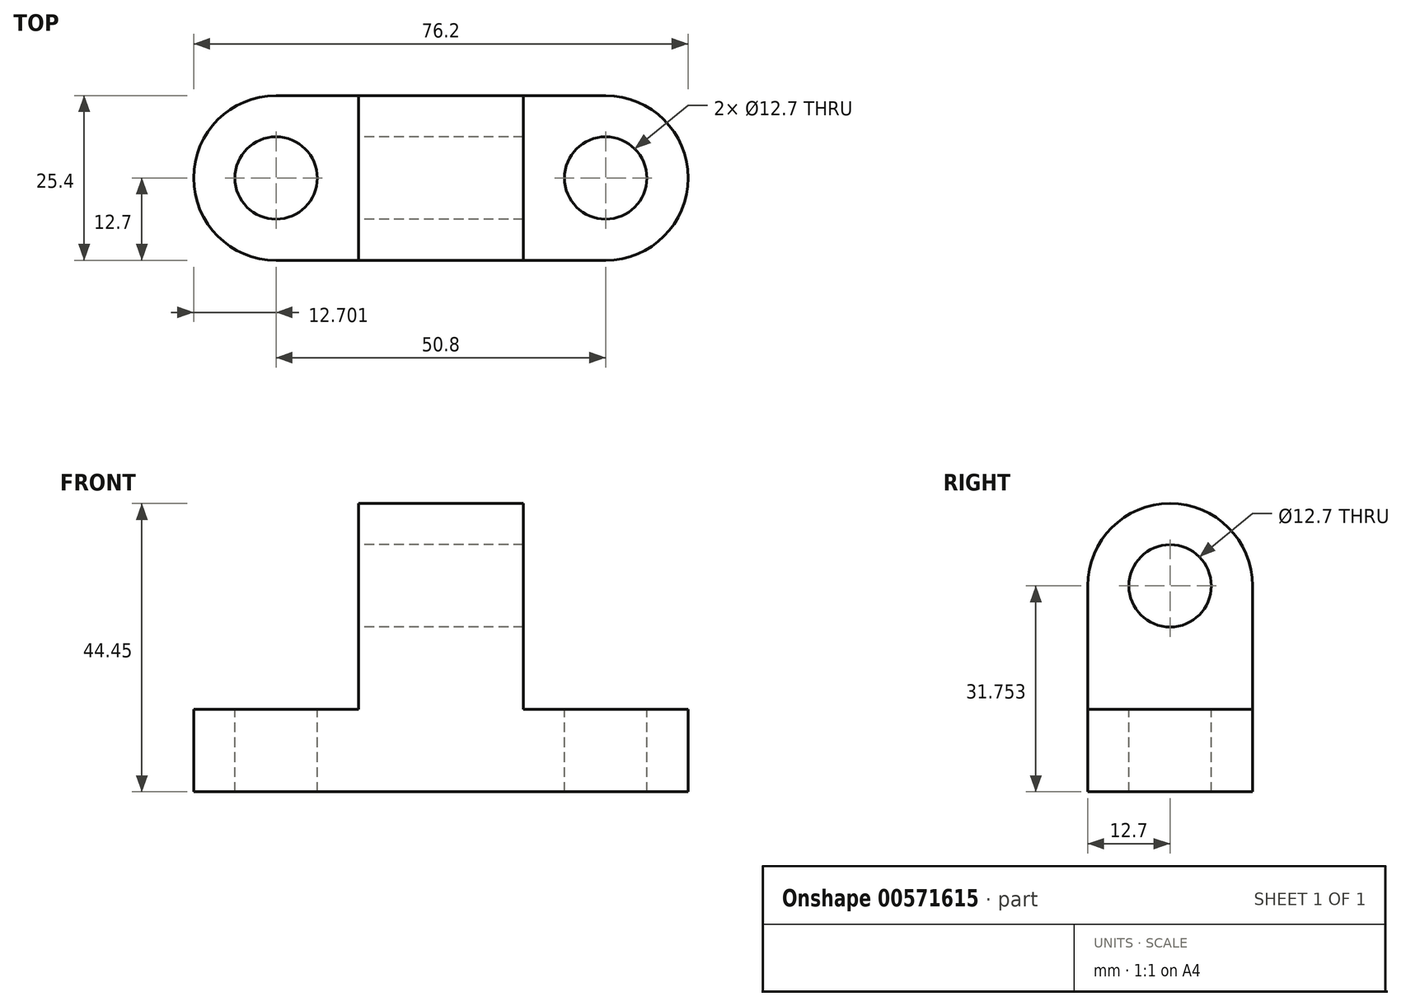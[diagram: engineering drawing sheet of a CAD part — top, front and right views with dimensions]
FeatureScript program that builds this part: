
annotation { "Feature Type Name" : "Feature", "Feature Type Description" : "" }
export const myFeature = defineFeature(function(context is Context, id is Id, definition is map)
    precondition{}
    {
        {
            var Q0;
            Q0=qCreatedBy(makeId("Front.planeOp"),FACE);
            var sketch = newSketch(context, id + "F0", { "sketchPlane" : qUnion([Q0])});
            skLineSegment(sketch, "E0", {"start": v(-37.6, -9.17) * mm, "end": v(13.2, -9.17) * mm});
            skLineSegment(sketch, "E1", {"start": v(13.2, -9.17) * mm, "end": v(13.2, 3.53) * mm});
            skLineSegment(sketch, "E2", {"start": v(13.2, 3.53) * mm, "end": v(0.5, 3.53) * mm});
            skLineSegment(sketch, "E3", {"start": v(0.5, 3.53) * mm, "end": v(0.5, 22.58) * mm});
            skLineSegment(sketch, "E4", {"start": v(0.5, 22.58) * mm, "end": v(-24.9, 22.58) * mm});
            skLineSegment(sketch, "E5", {"start": v(-24.9, 22.58) * mm, "end": v(-24.9, 3.53) * mm});
            skLineSegment(sketch, "E6", {"start": v(-24.9, 3.53) * mm, "end": v(-37.6, 3.53) * mm});
            skLineSegment(sketch, "E7", {"start": v(-37.6, 3.53) * mm, "end": v(-37.6, -9.17) * mm});
            skSolve(sketch);
        }
        {
            var Q0;
            Q0 = qSketchRegion(id + "F0", true);
            extrude(context, id + "F1", {"entities" : qUnion([Q0]), "depth" : 25.4 * mm, "offsetDistance" : 25.4 * mm});
        }
        {
            var Q0;
            Q0=makeQuery(id+"F1.opExtrude","SWEPT_FACE",FACE,{"disambiguationData":[OSD([sQuery(id+"F0.wireOp",EDGE,"E2")])]});
            var sketch = newSketch(context, id + "F2", { "sketchPlane" : qUnion([Q0])});
            skArc(sketch, "E8", {"start": v(13.2, -25.4) * mm, "mid": v(25.9, -12.7) * mm, "end": v(13.2, 0) * mm});
            skSolve(sketch);
        }
        {
            var Q0;
            Q0=makeQuery(id+"F2.imprint","IMPRINT",FACE,{"disambiguationData":[TD([[makeQuery(id+"F2.imprint","IMPRINT",EDGE,{"derivedFrom":sQuery(id+"F2.wireOp",EDGE,"E8")}),1.0]])]});
            extrude(context, id + "F3", {"entities" : qUnion([Q0]), "operationType" : NewBodyOperationType.ADD, "oppositeDirection" : true, "depth" : 12.7 * mm, "offsetDistance" : 25.4 * mm});
        }
        {
            var Q0;
            Q0=makeQuery(id+"F1.opExtrude","SWEPT_FACE",FACE,{"disambiguationData":[OSD([sQuery(id+"F0.wireOp",EDGE,"E6")])]});
            var sketch = newSketch(context, id + "F4", { "sketchPlane" : qUnion([Q0])});
            skArc(sketch, "E9", {"start": v(-37.6, 0) * mm, "mid": v(-50.3, -12.7) * mm, "end": v(-37.6, -25.4) * mm});
            skSolve(sketch);
        }
        {
            var Q0;
            Q0=makeQuery(id+"F4.imprint","IMPRINT",FACE,{"disambiguationData":[TD([[makeQuery(id+"F4.imprint","IMPRINT",EDGE,{"derivedFrom":sQuery(id+"F4.wireOp",EDGE,"E9")}),1.0]])]});
            extrude(context, id + "F5", {"entities" : qUnion([Q0]), "operationType" : NewBodyOperationType.ADD, "oppositeDirection" : true, "depth" : 12.7 * mm, "offsetDistance" : 25.4 * mm});
        }
        {
            var Q0;
            Q0=makeQuery(id+"F1.opExtrude","SWEPT_FACE",FACE,{"disambiguationData":[OSD([sQuery(id+"F0.wireOp",EDGE,"E5")])]});
            var sketch = newSketch(context, id + "F6", { "sketchPlane" : qUnion([Q0])});
            skArc(sketch, "E10", {"start": v(25.4, 22.58) * mm, "mid": v(12.7, 35.28) * mm, "end": v(0, 22.58) * mm});
            skSolve(sketch);
        }
        {
            var Q0;
            Q0 = qSketchRegion(id + "F6", true);
            var Q1;
            Q1=makeQuery(id+"F6.imprint","IMPRINT",FACE,{"disambiguationData":[TD([[makeQuery(id+"F6.imprint","IMPRINT",EDGE,{"derivedFrom":sQuery(id+"F6.wireOp",EDGE,"E10")}),1.0]])]});
            extrude(context, id + "F7", {"entities" : qUnion([Q0, Q1]), "operationType" : NewBodyOperationType.ADD, "oppositeDirection" : true, "depth" : 25.4 * mm, "offsetDistance" : 25.4 * mm});
        }
        {
            var Q0;
            {var subQ0=sQuery(id+"F0.wireOp",EDGE,"E5");Q0=makeQuery(id+"F7.boolean.opBoolean","MERGE",FACE,{"derivedFrom":[makeQuery(id+"F1.opExtrude","SWEPT_FACE",FACE,{"disambiguationData":[OSD([subQ0])]}),makeQuery(id+"F7.opExtrude","CAP_FACE",FACE,{"disambiguationData":[OSD([sQuery(id+"F0.wireOp",EDGE,"E4"),subQ0,sQuery(id+"F6.wireOp",EDGE,"E10")])],"isStart":true})]});}
            var sketch = newSketch(context, id + "F8", { "sketchPlane" : qUnion([Q0])});
            skCircle(sketch, "E11", {"center": v(12.7, 22.58) * mm, "radius": 6.35 * mm});
            skSolve(sketch);
        }
        {
            var Q0;
            Q0=makeQuery(id+"F8.imprint","IMPRINT",FACE,{"disambiguationData":[TD([[makeQuery(id+"F8.imprint","IMPRINT",EDGE,{"derivedFrom":sQuery(id+"F8.wireOp",EDGE,"E11")}),1.0]])]});
            var Q1;
            Q1=sQuery(id+"F8.wireOp",EDGE,"E11");
            extrude(context, id + "F9", {"entities" : qUnion([Q0]), "operationType" : NewBodyOperationType.REMOVE, "surfaceEntities" : qUnion([Q1]), "oppositeDirection" : true, "depth" : 25.4 * mm, "offsetDistance" : 25.4 * mm});
        }
        {
            var Q0;
            {var subQ0=sQuery(id+"F0.wireOp",EDGE,"E6");Q0=makeQuery(id+"F5.boolean.opBoolean","MERGE",FACE,{"derivedFrom":[makeQuery(id+"F1.opExtrude","SWEPT_FACE",FACE,{"disambiguationData":[OSD([subQ0])]}),makeQuery(id+"F5.opExtrude","CAP_FACE",FACE,{"disambiguationData":[OSD([subQ0,sQuery(id+"F0.wireOp",EDGE,"E7"),sQuery(id+"F4.wireOp",EDGE,"E9")])],"isStart":true})]});}
            var sketch = newSketch(context, id + "F10", { "sketchPlane" : qUnion([Q0])});
            skCircle(sketch, "E12", {"center": v(-37.6, -12.7) * mm, "radius": 6.35 * mm});
            skSolve(sketch);
        }
        {
            var Q0;
            {var subQ0=sQuery(id+"F0.wireOp",EDGE,"E2");Q0=makeQuery(id+"F3.boolean.opBoolean","MERGE",FACE,{"derivedFrom":[makeQuery(id+"F1.opExtrude","SWEPT_FACE",FACE,{"disambiguationData":[OSD([subQ0])]}),makeQuery(id+"F3.opExtrude","CAP_FACE",FACE,{"disambiguationData":[OSD([sQuery(id+"F0.wireOp",EDGE,"E1"),subQ0,sQuery(id+"F2.wireOp",EDGE,"E8")])],"isStart":true})]});}
            var sketch = newSketch(context, id + "F11", { "sketchPlane" : qUnion([Q0])});
            skCircle(sketch, "E13", {"center": v(13.2, -12.7) * mm, "radius": 6.35 * mm});
            skSolve(sketch);
        }
        {
            var Q0;
            Q0=makeQuery(id+"F10.imprint","IMPRINT",FACE,{"disambiguationData":[TD([[makeQuery(id+"F10.imprint","IMPRINT",EDGE,{"derivedFrom":sQuery(id+"F10.wireOp",EDGE,"E12")}),1.0]])]});
            extrude(context, id + "F12", {"entities" : qUnion([Q0]), "operationType" : NewBodyOperationType.REMOVE, "oppositeDirection" : true, "depth" : 25.4 * mm, "offsetDistance" : 25.4 * mm});
        }
        {
            var Q0;
            Q0=makeQuery(id+"F11.imprint","IMPRINT",FACE,{"disambiguationData":[TD([[makeQuery(id+"F11.imprint","IMPRINT",EDGE,{"derivedFrom":sQuery(id+"F11.wireOp",EDGE,"E13")}),1.0]])]});
            extrude(context, id + "F13", {"entities" : qUnion([Q0]), "operationType" : NewBodyOperationType.REMOVE, "oppositeDirection" : true, "depth" : 25.4 * mm, "offsetDistance" : 25.4 * mm});
        }
    });
